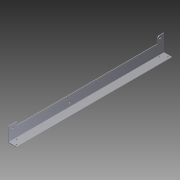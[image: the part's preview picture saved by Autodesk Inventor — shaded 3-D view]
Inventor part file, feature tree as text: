
AUTODESK INVENTOR PART (.ipt)
format: ipt  version: 2012 (Build 160160000, 160)  size: 120,320 bytes
history: native  units: in
note: dims shown in document units (in); Inventor stores cm internally (conversion verified against a paired STEP export)
features: extrude x3, sketch x3
ambient origin geometry x8: Origin, YZ Plane, XZ Plane, XY Plane, X Axis, Y Axis, Z Axis, Center Point
bodies: Solid1 (feature_tree)
feature tree (6):
  extrude  "Extrusion1"  Depth=0.0625in
  extrude  "Extrusion2"  Depth=2.0in
  extrude  "Extrusion3"  Depth=0.75in
  sketch  "Sketch1"  dims[d0=0.0625in d1=0.0625in]
  sketch  "Sketch2"  dims[d2=1.0in d3=2.0in]
  sketch  "Sketch3"  dims[d4=18.0in d5=0.0in d6=0.75in d7=0.75in d8=0.25in d9=0.5in d10=0.25in d11=1.0in d12=0.0in d13=0.875in d14=1.0in d15=0.2in d16=1.25in d17=0.5in d18=0.375in d19=0.5in d20=0.125in d21=0.25in d22=0.25in d23=0.75in d24=0.25in d25=1.0in d26=0.0in d27=7.5in]
